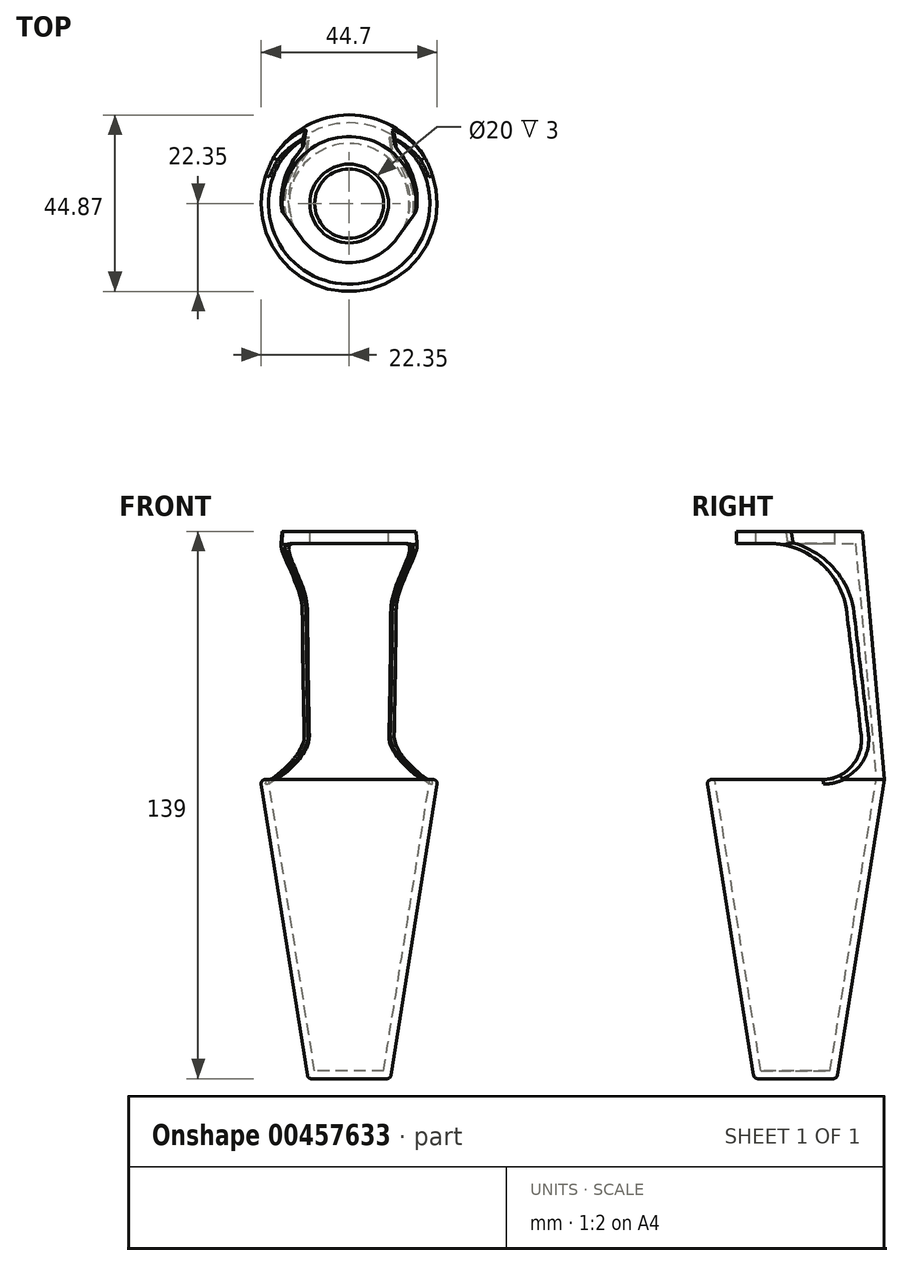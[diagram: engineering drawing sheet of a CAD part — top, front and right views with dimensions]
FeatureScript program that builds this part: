
annotation { "Feature Type Name" : "Feature", "Feature Type Description" : "" }
export const myFeature = defineFeature(function(context is Context, id is Id, definition is map)
    precondition{}
    {
        {
            var Q0;
            Q0=qCreatedBy(makeId("Front.planeOp"),FACE);
            var sketch = newSketch(context, id + "F0", { "sketchPlane" : qUnion([Q0])});
            skLineSegment(sketch, "E0", {"start": v(0, 60) * mm, "end": v(0, 0) * mm, "construction": true});
            skLineSegment(sketch, "E1", {"start": v(0, 60) * mm, "end": v(0, 63) * mm});
            skLineSegment(sketch, "E2", {"start": v(0, 63) * mm, "end": v(17, 63) * mm});
            skLineSegment(sketch, "E3", {"start": v(17, 63) * mm, "end": v(22.52, 0) * mm});
            skLineSegment(sketch, "E4", {"start": v(22.52, 0) * mm, "end": v(10.49, -76) * mm});
            skLineSegment(sketch, "E5", {"start": v(10.49, -76) * mm, "end": v(0, -76) * mm});
            skLineSegment(sketch, "E6", {"start": v(0, 60) * mm, "end": v(15.24, 60) * mm});
            skLineSegment(sketch, "E7", {"start": v(15.24, 60) * mm, "end": v(20.5, 0) * mm});
            skLineSegment(sketch, "E8", {"start": v(20.5, 0) * mm, "end": v(8.78, -74) * mm});
            skLineSegment(sketch, "E9", {"start": v(8.78, -74) * mm, "end": v(0, -74) * mm});
            skLineSegment(sketch, "E10", {"start": v(0, -76) * mm, "end": v(0, -74) * mm});
            skSolve(sketch);
        }
        {
            var Q0;
            Q0=makeQuery(id+"F0.imprint","IMPRINT",FACE,{"disambiguationData":[TD([[makeQuery(id+"F0.imprint","IMPRINT",EDGE,{"derivedFrom":sQuery(id+"F0.wireOp",EDGE,"E1")}),-1.0]])]});
            var Q1;
            Q1=sQuery(id+"F0.wireOp",EDGE,"E0");
            revolve(context, id + "F1", {"entities" : qUnion([Q0]), "axis" : qUnion([Q1]), "revolveType" : RevolveType.FULL});
        }
        {
            var Q0;
            Q0=qCreatedBy(makeId("Front.planeOp"),FACE);
            var sketch = newSketch(context, id + "F2", { "sketchPlane" : qUnion([Q0])});
            skLineSegment(sketch, "E11.0", {"start": v(15.24, 60) * mm, "end": v(20.5, 0) * mm});
            skLineSegment(sketch, "E12.0", {"start": v(17.26, 60) * mm, "end": v(22.52, 0) * mm});
            skLineSegment(sketch, "E13", {"start": v(20.5, 0) * mm, "end": v(22.52, 0) * mm});
            skLineSegment(sketch, "E14", {"start": v(15.24, 60) * mm, "end": v(17.26, 60) * mm});
            skPoint(sketch, "E15.orphan", {"position": v(17, 63) * mm});
            skSolve(sketch);
        }
        {
            var Q0;
            Q0 = qSketchRegion(id + "F2", true);
            var Q1;
            Q1=sQuery(id+"F0.wireOp",EDGE,"E0");
            revolve(context, id + "F3", {"operationType" : NewBodyOperationType.REMOVE, "entities" : qUnion([Q0]), "axis" : qUnion([Q1]), "revolveType" : RevolveType.ONE_DIRECTION, "angle" : 180 * degree});
        }
        {
            var Q0;
            Q0=qCreatedBy(makeId("Right.planeOp"),FACE);
            var sketch = newSketch(context, id + "F4", { "sketchPlane" : qUnion([Q0])});
            skLineSegment(sketch, "E16", {"start": v(0, 60) * mm, "end": v(11, 60) * mm});
            skLineSegment(sketch, "E17", {"start": v(0, 60) * mm, "end": v(0, 0) * mm});
            skLineSegment(sketch, "E18", {"start": v(0, 0) * mm, "end": v(18, 0) * mm});
            skLineSegment(sketch, "E19", {"start": v(18, 0) * mm, "end": v(11, 60) * mm});
            skSolve(sketch);
        }
        {
            var Q0;
            Q0 = qSketchRegion(id + "F4", true);
            extrude(context, id + "F5", {"entities" : qUnion([Q0]), "operationType" : NewBodyOperationType.REMOVE, "endBound" : BoundingType.SYMMETRIC, "depth" : 55 * mm});
        }
        {
            var Q0;
            Q0=makeQuery(id+"F5.boolean.opBoolean","COPY",EDGE,{"disambiguationData":[OD(1.0)],"derivedFrom":makeQuery(id+"F5.opExtrude","SWEPT_EDGE",EDGE,{"disambiguationData":[OSD([sQuery(id+"F4.wireOp",EDGE,"E18"),sQuery(id+"F4.wireOp",EDGE,"E19")])]})});
            var Q1;
            Q1=makeQuery(id+"F5.boolean.opBoolean","COPY",EDGE,{"disambiguationData":[OD(0.0)],"derivedFrom":makeQuery(id+"F5.opExtrude","SWEPT_EDGE",EDGE,{"disambiguationData":[OSD([sQuery(id+"F4.wireOp",EDGE,"E18"),sQuery(id+"F4.wireOp",EDGE,"E19")])]})});
            fillet(context, id + "F6", {"entities" : qUnion([Q0, Q1]), "radius" : 10 * mm, "tangentPropagation" : true, "allowEdgeOverflow" : false});
        }
        {
            var Q0;
            Q0=makeQuery(id+"F5.boolean.opBoolean","COPY",EDGE,{"disambiguationData":[OD(1.0)],"derivedFrom":makeQuery(id+"F5.opExtrude","SWEPT_EDGE",EDGE,{"disambiguationData":[OSD([sQuery(id+"F4.wireOp",EDGE,"E16"),sQuery(id+"F4.wireOp",EDGE,"E19")])]})});
            var Q1;
            Q1=makeQuery(id+"F5.boolean.opBoolean","COPY",EDGE,{"disambiguationData":[OD(0.0)],"derivedFrom":makeQuery(id+"F5.opExtrude","SWEPT_EDGE",EDGE,{"disambiguationData":[OSD([sQuery(id+"F4.wireOp",EDGE,"E16"),sQuery(id+"F4.wireOp",EDGE,"E19")])]})});
            fillet(context, id + "F7", {"entities" : qUnion([Q0, Q1]), "radius" : 20 * mm, "tangentPropagation" : true, "allowEdgeOverflow" : false});
        }
        {
            var Q0;
            Q0=makeQuery(id+"F7.opFillet","BLEND_EDGE",EDGE,{"blendedFrom":[makeQuery(id+"F5.boolean.opBoolean","COPY",EDGE,{"disambiguationData":[OD(0.0)],"derivedFrom":makeQuery(id+"F5.opExtrude","SWEPT_EDGE",EDGE,{"disambiguationData":[OSD([sQuery(id+"F4.wireOp",EDGE,"E16"),sQuery(id+"F4.wireOp",EDGE,"E19")])]})}),makeQuery(id+"F1.opRevolve","SWEPT_FACE",FACE,{"disambiguationData":[OSD([sQuery(id+"F0.wireOp",EDGE,"E3")])]})],"blendedInto":[makeQuery(id+"F1.opRevolve","SWEPT_FACE",FACE,{"disambiguationData":[OSD([sQuery(id+"F0.wireOp",EDGE,"E3")])]})]});
            var Q1;
            {var subQ0=makeQuery(id+"F1.opRevolve","SWEPT_EDGE",EDGE,{"disambiguationData":[OSD([sQuery(id+"F0.wireOp",EDGE,"E3"),sQuery(id+"F0.wireOp",EDGE,"E4")])]});Q1=makeQuery(id+"F5.boolean.opBoolean","MERGE",EDGE,{"derivedFrom":[makeQuery(id+"F3.boolean.opBoolean","MERGE",EDGE,{"derivedFrom":[subQ0,makeQuery(id+"F3.opRevolve","SWEPT_EDGE",EDGE,{"disambiguationData":[OSD([sQuery(id+"F2.wireOp",EDGE,"E12.0"),sQuery(id+"F2.wireOp",EDGE,"E13")])]})]}),makeQuery(id+"F3.boolean.opBoolean","SPLIT",EDGE,{"derivedFrom":subQ0})]});}
            var Q2;
            Q2=makeQuery(id+"F1.opRevolve","SWEPT_EDGE",EDGE,{"disambiguationData":[OSD([sQuery(id+"F0.wireOp",EDGE,"E4"),sQuery(id+"F0.wireOp",EDGE,"E5")])]});
            fillet(context, id + "F8", {"entities" : qUnion([Q0, Q1, Q2]), "radius" : 1 * mm, "tangentPropagation" : true, "allowEdgeOverflow" : false});
        }
        {
            var Q0;
            Q0=makeQuery(id+"F1.opRevolve","SWEPT_FACE",FACE,{"disambiguationData":[OSD([sQuery(id+"F0.wireOp",EDGE,"E2")])]});
            var sketch = newSketch(context, id + "F9", { "sketchPlane" : qUnion([Q0])});
            skCircle(sketch, "E20", {"center": v(0, 0) * mm, "radius": 10 * mm});
            skSolve(sketch);
        }
        {
            var Q0;
            Q0 = qSketchRegion(id + "F9", true);
            extrude(context, id + "F10", {"entities" : qUnion([Q0]), "operationType" : NewBodyOperationType.REMOVE, "oppositeDirection" : true, "depth" : 5 * mm, "offsetDistance" : 25 * mm});
        }
        {
            var Q0;
            Q0=makeQuery(id+"F1.opRevolve","SWEPT_FACE",FACE,{"disambiguationData":[OSD([sQuery(id+"F0.wireOp",EDGE,"E2")])]});
            var sketch = newSketch(context, id + "F11", { "sketchPlane" : qUnion([Q0])});
            skArc(sketch, "E21", {"start": v(0, -15) * mm, "mid": v(6.8, -13.37) * mm, "end": v(12.14, -8.82) * mm});
            skLineSegment(sketch, "E22", {"start": v(19.7, 1.6) * mm, "end": v(12.14, -8.82) * mm});
            skLineSegment(sketch, "E23", {"start": v(23.24, -18.97) * mm, "end": v(0, -25.63) * mm});
            skLineSegment(sketch, "E24", {"start": v(19.7, 1.6) * mm, "end": v(23.24, -18.97) * mm});
            skLineSegment(sketch, "E25", {"start": v(0, 0) * mm, "end": v(0, -15) * mm, "construction": true});
            skPoint(sketch, "E26.start.orphan", {"position": v(-17, 0) * mm});
            skLineSegment(sketch, "E27.MirrorCS", {"start": v(-23.24, -18.97) * mm, "end": v(0, -25.63) * mm});
            skArc(sketch, "E28.MirrorCS", {"start": v(0, -15) * mm, "mid": v(-6.8, -13.37) * mm, "end": v(-12.14, -8.82) * mm});
            skLineSegment(sketch, "E29.MirrorCS", {"start": v(-19.7, 1.6) * mm, "end": v(-12.14, -8.82) * mm});
            skLineSegment(sketch, "E30.MirrorCS", {"start": v(-19.7, 1.6) * mm, "end": v(-23.24, -18.97) * mm});
            skSolve(sketch);
        }
        {
            var Q0;
            Q0=makeQuery(id+"F11.imprint","IMPRINT",FACE,{"disambiguationData":[TD([[makeQuery(id+"F11.imprint","IMPRINT",EDGE,{"derivedFrom":sQuery(id+"F11.wireOp",EDGE,"E23")}),-1.0]])]});
            var Q1;
            Q1=makeQuery(id+"F11.imprint","IMPRINT",FACE,{"disambiguationData":[TD([[makeQuery(id+"F11.imprint","IMPRINT",EDGE,{"derivedFrom":sQuery(id+"F11.wireOp",EDGE,"E21")}),-1.0]])]});
            extrude(context, id + "F12", {"entities" : qUnion([Q0, Q1]), "operationType" : NewBodyOperationType.REMOVE, "oppositeDirection" : true, "depth" : 15 * mm, "offsetDistance" : 25 * mm});
        }
        {
            var Q0;
            Q0=makeQuery(id+"F12.boolean.opBoolean","INTERSECT",EDGE,{"derivedFrom":[makeQuery(id+"F1.opRevolve","SWEPT_FACE",FACE,{"disambiguationData":[OSD([sQuery(id+"F0.wireOp",EDGE,"E3")])]}),makeQuery(id+"F12.opExtrude","SWEPT_FACE",FACE,{"disambiguationData":[OSD([sQuery(id+"F11.wireOp",EDGE,"E22"),sQuery(id+"F11.wireOp",EDGE,"kLoqPunC-dOfU-TKPz-Pnu8-qVxWjo3u3uOn")])]})]});
            var Q1;
            Q1=makeQuery(id+"F12.boolean.opBoolean","INTERSECT",EDGE,{"derivedFrom":[makeQuery(id+"F1.opRevolve","SWEPT_FACE",FACE,{"disambiguationData":[OSD([sQuery(id+"F0.wireOp",EDGE,"E3")])]}),makeQuery(id+"F12.opExtrude","SWEPT_FACE",FACE,{"disambiguationData":[OSD([sQuery(id+"F11.wireOp",EDGE,"E26"),sQuery(id+"F11.wireOp",EDGE,"R9R19m8k-B3BH-idtR-Ydt9-WVIZm6Ay6TTq")])]})]});
            fillet(context, id + "F13", {"entities" : qUnion([Q0, Q1]), "radius" : 4 * mm, "allowEdgeOverflow" : false});
        }
    });
